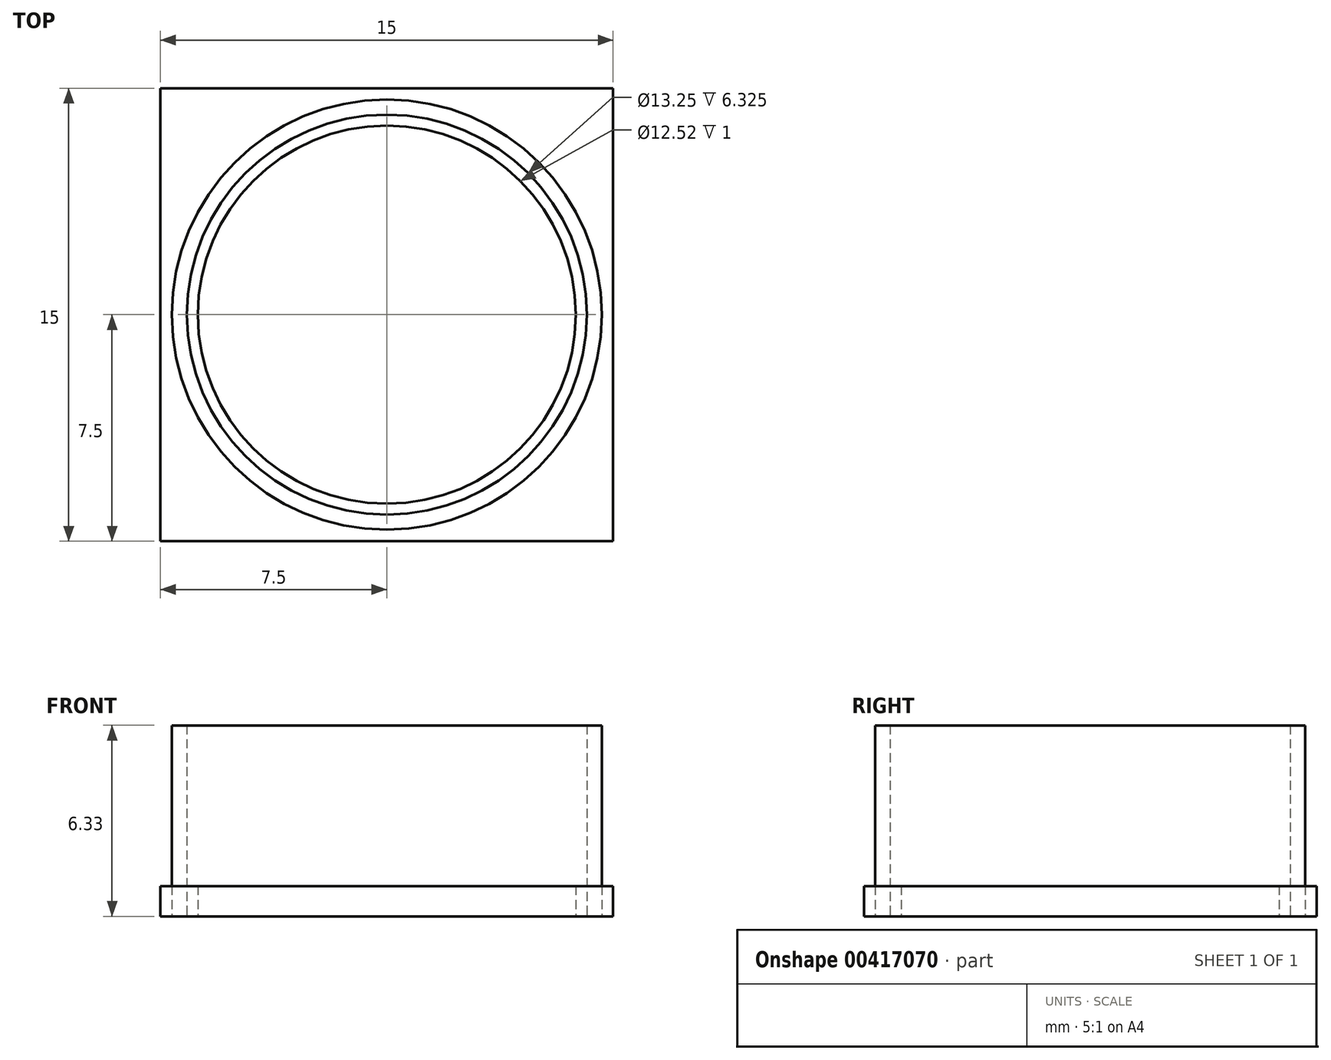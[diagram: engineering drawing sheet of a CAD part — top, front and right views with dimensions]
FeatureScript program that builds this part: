
annotation { "Feature Type Name" : "Feature", "Feature Type Description" : "" }
export const myFeature = defineFeature(function(context is Context, id is Id, definition is map)
    precondition{}
    {
        {
            var Q0;
            Q0=qCreatedBy(makeId("Top.planeOp"),FACE);
            var sketch = newSketch(context, id + "F0", { "sketchPlane" : qUnion([Q0])});
            skLineSegment(sketch, "E0.bottom", {"start": v(7.5, -7.5) * mm, "end": v(-7.5, -7.5) * mm});
            skLineSegment(sketch, "E0.top", {"start": v(7.5, 7.5) * mm, "end": v(-7.5, 7.5) * mm});
            skLineSegment(sketch, "E0.left", {"start": v(7.5, -7.5) * mm, "end": v(7.5, 7.5) * mm});
            skLineSegment(sketch, "E0.right", {"start": v(-7.5, -7.5) * mm, "end": v(-7.5, 7.5) * mm});
            skPoint(sketch, "E0.middle", {"position": v(0, 0) * mm});
            skCircle(sketch, "E1", {"center": v(0, 0) * mm, "radius": 6.26 * mm});
            skSolve(sketch);
        }
        {
            var Q0;
            Q0=makeQuery(id+"F0.imprint","IMPRINT",FACE,{"disambiguationData":[TD([[makeQuery(id+"F0.imprint","IMPRINT",EDGE,{"derivedFrom":sQuery(id+"F0.wireOp",EDGE,"E0.bottom")}),-1.0]])]});
            extrude(context, id + "F1", {"entities" : qUnion([Q0]), "depth" : 1 * mm});
        }
        {
            var Q0;
            Q0=qCreatedBy(makeId("Top.planeOp"),FACE);
            var sketch = newSketch(context, id + "F2", { "sketchPlane" : qUnion([Q0])});
            skCircle(sketch, "E2", {"center": v(0, 0) * mm, "radius": 6.62 * mm});
            skCircle(sketch, "E3", {"center": v(0, 0) * mm, "radius": 7.12 * mm});
            skSolve(sketch);
        }
        {
            var Q0;
            Q0=makeQuery(id+"F2.imprint","IMPRINT",FACE,{"disambiguationData":[TD([[makeQuery(id+"F2.imprint","IMPRINT",EDGE,{"derivedFrom":sQuery(id+"F2.wireOp",EDGE,"E2")}),-1.0]])]});
            extrude(context, id + "F3", {"entities" : qUnion([Q0]), "depth" : 6.33 * mm});
        }
    });
